# Revit family: 22 SMARTLIGHT
name_source: partatom
category: Furniture
units: mm (PartAtom-declared; Revit-internal decimal feet)

## family parameters
Always vertical = Yes
Cut with Voids When Loaded = No
Room Calculation Point = Yes
Shared = No
Work Plane-Based = Yes

## types (48) — shared parameters
Default Elevation = 1219 mm
Seat_00 = Seat_00
Structure_00 = Structure_00
Structure_01 = Structure_01

## per-type parameters (varying)
| type | Armstand_00 | Bar_sincro02 | Base_00 | Base_01 | Base_02 | Base_03 | Seat_Height | Struct_00 | Struct_01 | Synchron_00 | Synchron_01 | Synchron_02 | dist | leg_sincro |
| EX 1_4EXDI02 | Yes | No | Yes | No | No | No | 525 mm | Yes | No | Yes | No | No | 337 mm | Yes |
| EX 1_4EXDI04 | Yes | No | Yes | No | No | No | 525 mm | Yes | No | Yes | No | No | 337 mm | Yes |
| EX 1_4EXDI06 | Yes | No | No | Yes | No | No | 525 mm | Yes | No | Yes | No | No | 337 mm | Yes |
| EX 1_4EXDI08 | Yes | No | No | Yes | No | No | 525 mm | Yes | No | Yes | No | No | 337 mm | Yes |
| EX 2_4EXGI02 | Yes | No | Yes | No | No | No | 525 mm | No | Yes | Yes | No | No | 337 mm | Yes |
| EX 2_4EXGI04 | Yes | No | Yes | No | No | No | 525 mm | No | Yes | Yes | No | No | 337 mm | Yes |
| EX 2_4EXGI06 | Yes | No | No | Yes | No | No | 525 mm | No | Yes | Yes | No | No | 337 mm | Yes |
| EX 2_4EXGI08 | Yes | No | No | Yes | No | No | 525 mm | No | Yes | Yes | No | No | 337 mm | Yes |
| EX 3_4EXGI10 | No | No | Yes | No | No | No | 525 mm | No | Yes | Yes | No | No | 337 mm | Yes |
| EX 3_4EXGI12 | No | No | Yes | No | No | No | 525 mm | No | Yes | Yes | No | No | 337 mm | Yes |
| EX 3_4EXGI14 | No | No | No | Yes | No | No | 525 mm | No | Yes | Yes | No | No | 337 mm | Yes |
| EX 3_4EXGI16 | No | No | No | Yes | No | No | 525 mm | No | Yes | Yes | No | No | 337 mm | Yes |
| EX 4_4EXDI12 | Yes | No | Yes | No | No | No | 457 mm  [stored 1.49934 ft] | Yes | No | No | Yes | No | 268 mm | Yes |
| EX 4_4EXDI14 | Yes | No | No | Yes | No | No | 457 mm  [stored 1.49934 ft] | Yes | No | No | Yes | No | 268 mm | Yes |
| EX 4_4EXDI16 | Yes | No | No | Yes | No | No | 457 mm  [stored 1.49934 ft] | Yes | No | No | Yes | No | 268 mm | Yes |
| EX 5_4EXGI18 | Yes | No | Yes | No | No | No | 457 mm  [stored 1.49934 ft] | No | Yes | No | Yes | No | 268 mm | Yes |
| EX 5_4EXGI20 | Yes | No | Yes | No | No | No | 457 mm  [stored 1.49934 ft] | No | Yes | No | Yes | No | 268 mm | Yes |
| EX 5_4EXGI22 | Yes | No | No | Yes | No | No | 457 mm  [stored 1.49934 ft] | No | Yes | No | Yes | No | 268 mm | Yes |
| EX 5_4EXGI24 | Yes | No | No | Yes | No | No | 457 mm  [stored 1.49934 ft] | No | Yes | No | Yes | No | 268 mm | Yes |
| EX 6_4EXGI26 | No | No | Yes | No | No | No | 457 mm  [stored 1.49934 ft] | No | Yes | No | Yes | No | 268 mm | Yes |
| EX 6_4EXGI28 | No | No | Yes | No | No | No | 457 mm  [stored 1.49934 ft] | No | Yes | No | Yes | No | 268 mm | Yes |
| EX 6_4EXGI30 | No | No | No | Yes | No | No | 457 mm  [stored 1.49934 ft] | No | Yes | No | Yes | No | 268 mm | Yes |
| EX 6_4EXGI32 | No | No | No | Yes | No | No | 457 mm  [stored 1.49934 ft] | No | Yes | No | Yes | No | 268 mm | Yes |
| EX 7_4EXDI18 | Yes | Yes | Yes | No | No | No | 457 mm  [stored 1.49934 ft] | Yes | No | No | No | Yes | 268 mm | Yes |
| EX 4_4EXDI10 | Yes | No | Yes | No | No | No | 457 mm  [stored 1.49934 ft] | Yes | No | No | Yes | No | 268 mm | Yes |
| EX 7_4EXDI20 | Yes | Yes | Yes | No | No | No | 457 mm  [stored 1.49934 ft] | Yes | No | No | No | Yes | 268 mm | Yes |
| EX 7_4EXDI22 | Yes | Yes | No | Yes | No | No | 457 mm  [stored 1.49934 ft] | Yes | No | No | No | Yes | 268 mm | Yes |
| EX 7_4EXDI24 | Yes | Yes | No | Yes | No | No | 457 mm  [stored 1.49934 ft] | Yes | No | No | No | Yes | 268 mm | Yes |
| EX 8_4EXGI34 | Yes | Yes | Yes | No | No | No | 457 mm  [stored 1.49934 ft] | No | Yes | No | No | Yes | 268 mm | Yes |
| EX 8_4EXGI36 | Yes | Yes | Yes | No | No | No | 457 mm  [stored 1.49934 ft] | No | Yes | No | No | Yes | 268 mm | Yes |
| EX 8_4EXGI38 | Yes | Yes | No | Yes | No | No | 457 mm  [stored 1.49934 ft] | No | Yes | No | No | Yes | 268 mm | Yes |
| EX 8_4EXGI40 | Yes | Yes | No | Yes | No | No | 457 mm  [stored 1.49934 ft] | No | Yes | No | No | Yes | 268 mm | Yes |
| EX 9_4EXGI42 | No | Yes | Yes | No | No | No | 457 mm  [stored 1.49934 ft] | No | Yes | No | No | Yes | 268 mm | Yes |
| EX 9_4EXGI44 | No | Yes | Yes | No | No | No | 457 mm  [stored 1.49934 ft] | No | Yes | No | No | Yes | 268 mm | Yes |
| EX 9_4EXGI46 | No | Yes | No | Yes | No | No | 457 mm  [stored 1.49934 ft] | No | Yes | No | No | Yes | 268 mm | Yes |
| EX 9_4EXGI48 | No | Yes | No | Yes | No | No | 457 mm  [stored 1.49934 ft] | No | Yes | No | No | Yes | 268 mm | Yes |
| EX12_4EXDI26 | Yes | No | No | No | Yes | No | 457 mm  [stored 1.49934 ft] | Yes | No | No | No | Yes | 268 mm | No |
| EX12_4EXDI28 | Yes | No | No | No | Yes | No | 457 mm  [stored 1.49934 ft] | Yes | No | No | No | Yes | 268 mm | No |
| EX14_4EXFI02 | Yes | No | No | No | Yes | No | 457 mm  [stored 1.49934 ft] | No | Yes | No | No | Yes | 268 mm | No |
| EX14_4EXFI04 | Yes | No | No | No | Yes | No | 457 mm  [stored 1.49934 ft] | No | Yes | No | No | Yes | 268 mm | No |
| EX13_4EXDI30 | Yes | No | No | No | No | Yes | 391 mm | Yes | No | No | No | No | 268 mm | No |
| EX13_4EXDI32 | Yes | No | No | No | No | Yes | 391 mm | Yes | No | No | No | No | 268 mm | No |
| EX15_4EXFI06 | Yes | No | No | No | No | Yes | 391 mm | No | Yes | No | No | No | 268 mm | No |
| EX15_4EXFI08 | Yes | No | No | No | No | Yes | 391 mm | No | Yes | No | No | No | 268 mm | No |
| EX16_4EXFI10 | No | No | No | No | Yes | No | 457 mm  [stored 1.49934 ft] | No | Yes | No | No | Yes | 268 mm | No |
| EX16_4EXFI12 | No | No | No | No | Yes | No | 457 mm  [stored 1.49934 ft] | No | Yes | No | No | Yes | 268 mm | No |
| EX17_4EXFI14 | No | No | No | No | No | Yes | 391 mm | No | Yes | No | No | No | 268 mm | No |
| EX17_4EXFI16 | No | No | No | No | No | Yes | 391 mm | No | Yes | No | No | No | 268 mm | No |

note: [stored X ft] marks values corroborated as IEEE doubles in the binary element streams (Revit-internal decimal feet)

## geometry (parser evidence)
native form markers: Sweep x6
no freeform markers — native parametric forms only
